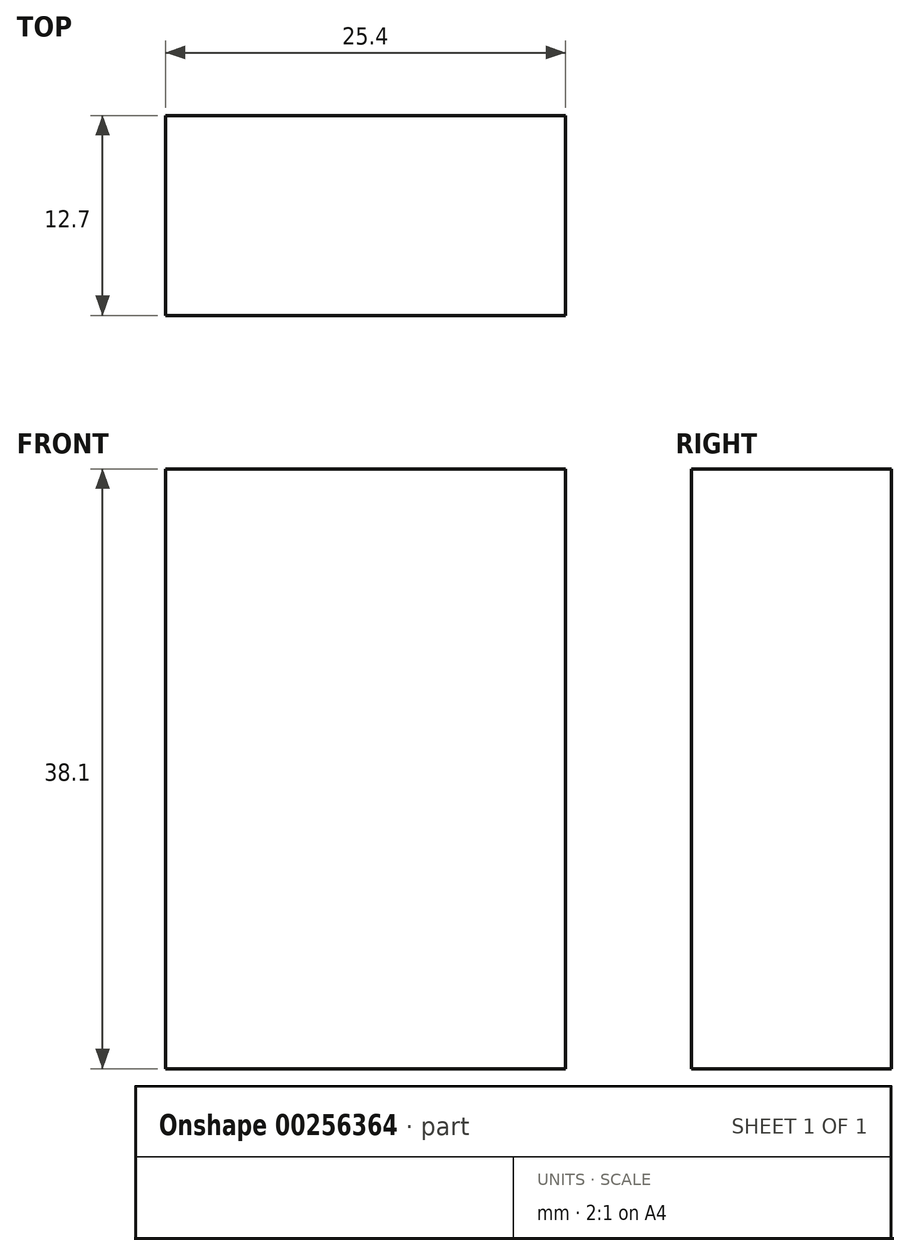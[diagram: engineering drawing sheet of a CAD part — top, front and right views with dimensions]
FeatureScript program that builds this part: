
annotation { "Feature Type Name" : "Feature", "Feature Type Description" : "" }
export const myFeature = defineFeature(function(context is Context, id is Id, definition is map)
    precondition{}
    {
        {
            var Q0;
            Q0=qCreatedBy(makeId("Front.planeOp"),FACE);
            var sketch = newSketch(context, id + "F0", { "sketchPlane" : qUnion([Q0])});
            skLineSegment(sketch, "E0", {"start": v(0, 0) * mm, "end": v(0, 38.1) * mm});
            skLineSegment(sketch, "E1", {"start": v(0, 38.1) * mm, "end": v(25.4, 38.1) * mm});
            skLineSegment(sketch, "E2", {"start": v(25.4, 38.1) * mm, "end": v(25.4, 0) * mm});
            skLineSegment(sketch, "E3", {"start": v(25.4, 0) * mm, "end": v(0, 0) * mm});
            skSolve(sketch);
        }
        {
            var Q0;
            Q0 = qSketchRegion(id + "F0", true);
            extrude(context, id + "F1", {"entities" : qUnion([Q0]), "depth" : 12.7 * mm});
        }
    });
